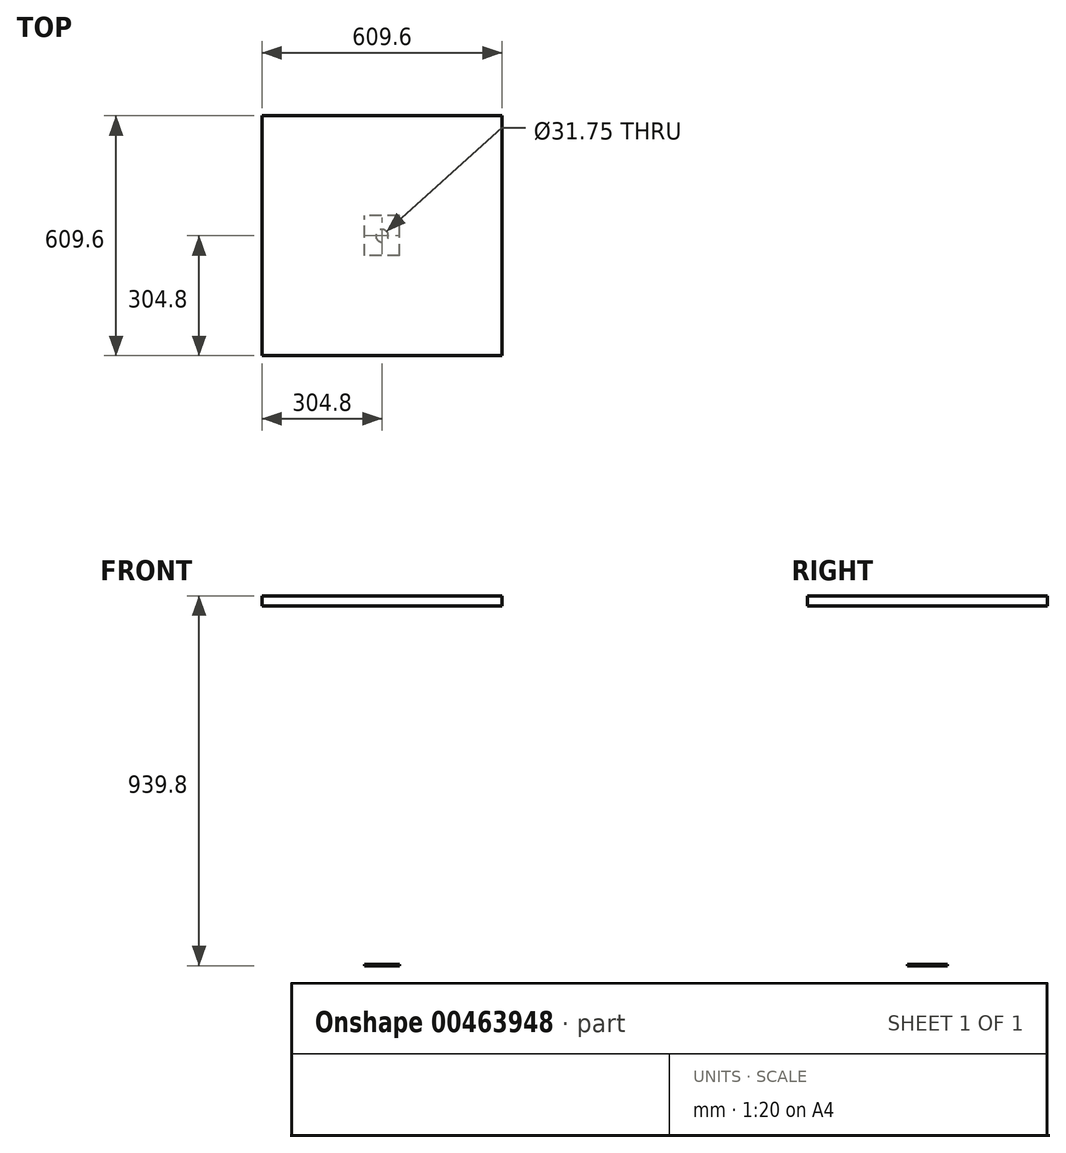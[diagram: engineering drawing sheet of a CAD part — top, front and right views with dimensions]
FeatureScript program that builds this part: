
annotation { "Feature Type Name" : "Feature", "Feature Type Description" : "" }
export const myFeature = defineFeature(function(context is Context, id is Id, definition is map)
    precondition{}
    {
        {
            var Q0;
            Q0=qCreatedBy(makeId("Top.planeOp"),FACE);
            var sketch = newSketch(context, id + "F0", { "sketchPlane" : qUnion([Q0])});
            skLineSegment(sketch, "E0.bottom", {"start": v(304.8, -304.8) * mm, "end": v(-304.8, -304.8) * mm});
            skLineSegment(sketch, "E0.top", {"start": v(304.8, 304.8) * mm, "end": v(-304.8, 304.8) * mm});
            skLineSegment(sketch, "E0.left", {"start": v(304.8, -304.8) * mm, "end": v(304.8, 304.8) * mm});
            skLineSegment(sketch, "E0.right", {"start": v(-304.8, -304.8) * mm, "end": v(-304.8, 304.8) * mm});
            skPoint(sketch, "E0.middle", {"position": v(0, 0) * mm});
            skSolve(sketch);
        }
        {
            var Q0;
            Q0=qCreatedBy(makeId("Top.planeOp"),FACE);
            cPlane(context, id + "F1", {"entities" : qUnion([Q0]), "cplaneType" : CPlaneType.OFFSET, "offset" : 965.2 * mm, "oppositeDirection" : true, "width" : 152.4 * mm, "height" : 152.4 * mm});
        }
        {
            var Q0;
            Q0=qCreatedBy(id+"F1.planeOp",FACE);
            var sketch = newSketch(context, id + "F2", { "sketchPlane" : qUnion([Q0])});
            skLineSegment(sketch, "E1.bottom", {"start": v(44.45, -50.8) * mm, "end": v(-44.45, -50.8) * mm});
            skLineSegment(sketch, "E1.top", {"start": v(44.45, 50.8) * mm, "end": v(-44.45, 50.8) * mm});
            skLineSegment(sketch, "E1.left", {"start": v(44.45, -50.8) * mm, "end": v(44.45, 50.8) * mm});
            skLineSegment(sketch, "E1.right", {"start": v(-44.45, -50.8) * mm, "end": v(-44.45, 50.8) * mm});
            skPoint(sketch, "E1.middle", {"position": v(0, 0) * mm});
            skSolve(sketch);
        }
        {
            var Q0;
            Q0=qCreatedBy(id+"F1.planeOp",FACE);
            cPlane(context, id + "F3", {"entities" : qUnion([Q0]), "cplaneType" : CPlaneType.OFFSET, "offset" : 50.8 * mm, "width" : 152.4 * mm, "height" : 152.4 * mm});
        }
        {
            var Q0;
            Q0=qCreatedBy(id+"F3.planeOp",FACE);
            var sketch = newSketch(context, id + "F4", { "sketchPlane" : qUnion([Q0])});
            skCircle(sketch, "E2", {"center": v(0, 0) * mm, "radius": 15.88 * mm});
            skSolve(sketch);
        }
        {
            var Q0;
            Q0=qCreatedBy(id+"F3.planeOp",FACE);
            var sketch = newSketch(context, id + "F5", { "sketchPlane" : qUnion([Q0])});
            skLineSegment(sketch, "E3.0", {"start": v(-44.45, -50.8) * mm, "end": v(-44.45, 50.8) * mm});
            skLineSegment(sketch, "E3.1", {"start": v(44.45, -50.8) * mm, "end": v(44.45, 50.8) * mm});
            skLineSegment(sketch, "E3.2", {"start": v(44.45, -50.8) * mm, "end": v(-44.45, -50.8) * mm});
            skLineSegment(sketch, "E3.3", {"start": v(44.45, 50.8) * mm, "end": v(-44.45, 50.8) * mm});
            skCircle(sketch, "E4.0", {"center": v(0, 0) * mm, "radius": 15.88 * mm});
            skSolve(sketch);
        }
        {
            var Q0;
            Q0=makeQuery(id+"F0.imprint","IMPRINT",FACE,{"disambiguationData":[TD([[makeQuery(id+"F0.imprint","IMPRINT",EDGE,{"derivedFrom":sQuery(id+"F0.wireOp",EDGE,"E0.bottom")}),-1.0]])]});
            extrude(context, id + "F6", {"entities" : qUnion([Q0]), "depth" : 25.4 * mm, "offsetDistance" : 25.4 * mm});
        }
        {
            var Q0;
            Q0=makeQuery(id+"F5.imprint","IMPRINT",FACE,{"disambiguationData":[TD([[makeQuery(id+"F5.imprint","IMPRINT",EDGE,{"derivedFrom":sQuery(id+"F5.wireOp",EDGE,"E3.0")}),-1.0]])]});
            extrude(context, id + "F7", {"entities" : qUnion([Q0]), "depth" : 3.17 * mm, "offsetDistance" : 25.4 * mm});
        }
    });
